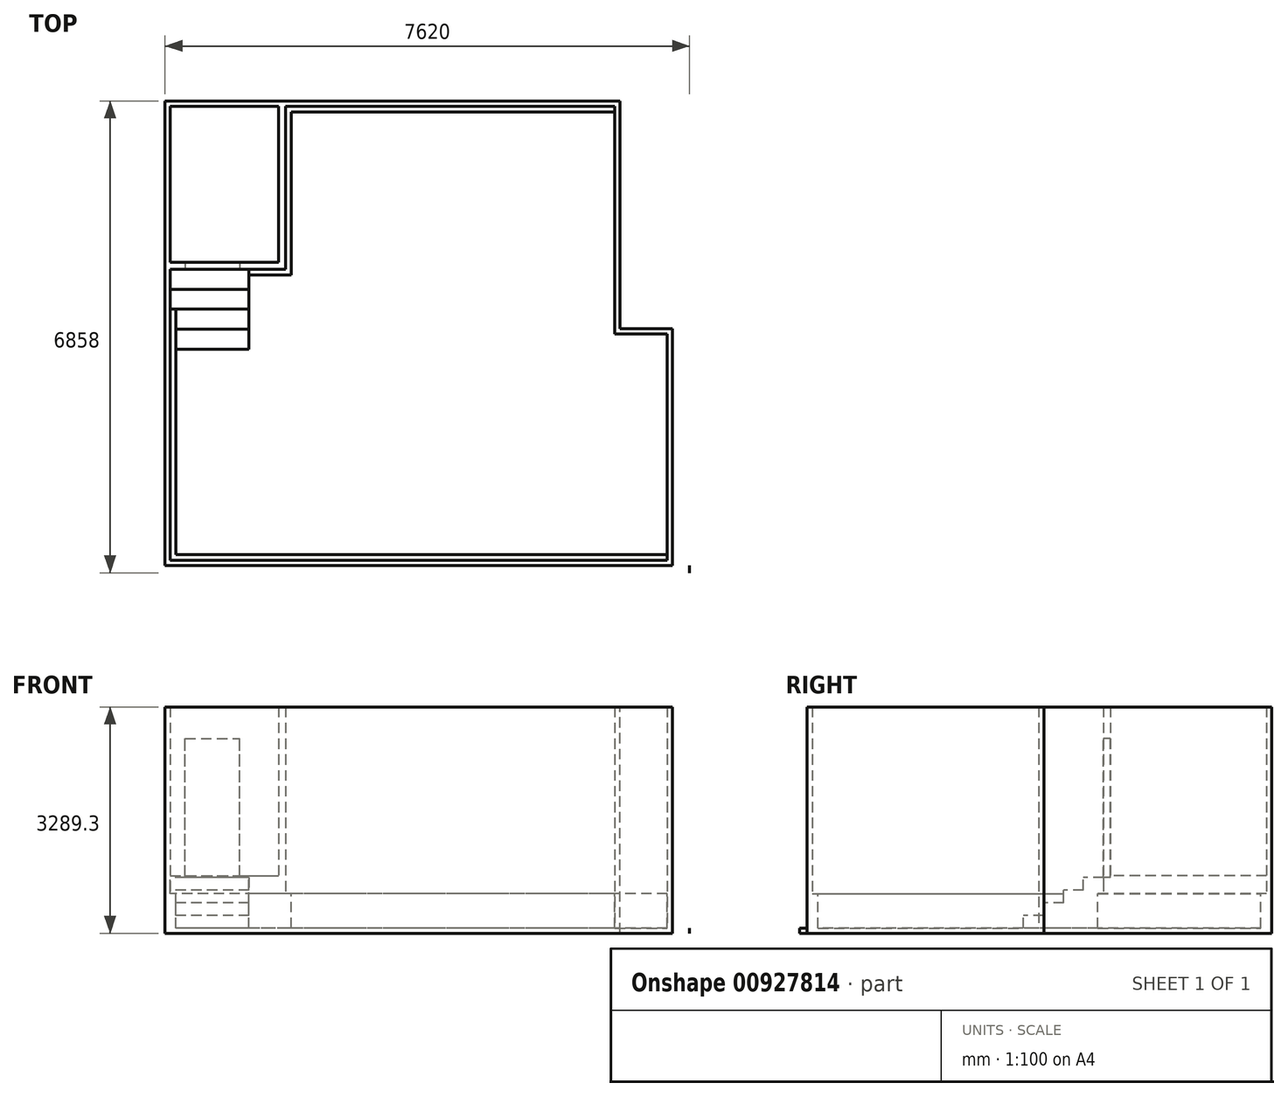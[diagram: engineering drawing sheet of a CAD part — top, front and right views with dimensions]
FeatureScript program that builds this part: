
annotation { "Feature Type Name" : "Feature", "Feature Type Description" : "" }
export const myFeature = defineFeature(function(context is Context, id is Id, definition is map)
    precondition{}
    {
        {
            var Q0;
            Q0=qCreatedBy(makeId("Top.planeOp"),FACE);
            var sketch = newSketch(context, id + "F0", { "sketchPlane" : qUnion([Q0])});
            skLineSegment(sketch, "E0.bottom", {"start": v(0, 0) * mm, "end": v(7620, 0) * mm});
            skLineSegment(sketch, "E0.top", {"start": v(0, -6858) * mm, "end": v(7620, -6858) * mm});
            skLineSegment(sketch, "E0.left", {"start": v(0, 0) * mm, "end": v(0, -6858) * mm});
            skLineSegment(sketch, "E0.right", {"start": v(7620, 0) * mm, "end": v(7620, -6858) * mm});
            skSolve(sketch);
        }
        {
            var Q0;
            Q0=makeQuery(id+"F0.imprint","IMPRINT",FACE,{"disambiguationData":[TD([[makeQuery(id+"F0.imprint","IMPRINT",EDGE,{"derivedFrom":sQuery(id+"F0.wireOp",EDGE,"E0.bottom")}),-1.0]])]});
            extrude(context, id + "F1", {"entities" : qUnion([Q0]), "oppositeDirection" : true, "depth" : 76.2 * mm, "offsetDistance" : 25.4 * mm});
        }
        {
            var Q0;
            Q0=makeQuery(id+"F1.opExtrude","CAP_FACE",FACE,{"disambiguationData":[OSD([sQuery(id+"F0.wireOp",EDGE,"E0.bottom"),sQuery(id+"F0.wireOp",EDGE,"E0.top"),sQuery(id+"F0.wireOp",EDGE,"E0.left"),sQuery(id+"F0.wireOp",EDGE,"E0.right")])],"isStart":true});
            var sketch = newSketch(context, id + "F2", { "sketchPlane" : qUnion([Q0])});
            skLineSegment(sketch, "E1.bottom", {"start": v(0, 0) * mm, "end": v(76.2, 0) * mm});
            skLineSegment(sketch, "E1.top", {"start": v(0, -6858) * mm, "end": v(76.2, -6858) * mm});
            skLineSegment(sketch, "E1.left", {"start": v(0, 0) * mm, "end": v(0, -6858) * mm});
            skLineSegment(sketch, "E1.right", {"start": v(76.2, 0) * mm, "end": v(76.2, -6858) * mm});
            skSolve(sketch);
        }
        {
            var Q0;
            Q0 = qSketchRegion(id + "F2", true);
            extrude(context, id + "F3", {"entities" : qUnion([Q0]), "operationType" : NewBodyOperationType.ADD, "depth" : 3213.1 * mm, "offsetDistance" : 25.4 * mm});
        }
        {
            var Q0;
            Q0=makeQuery(id+"F1.opExtrude","CAP_FACE",FACE,{"disambiguationData":[OSD([sQuery(id+"F0.wireOp",EDGE,"E0.bottom"),sQuery(id+"F0.wireOp",EDGE,"E0.top"),sQuery(id+"F0.wireOp",EDGE,"E0.left"),sQuery(id+"F0.wireOp",EDGE,"E0.right")])],"isStart":true});
            var sketch = newSketch(context, id + "F4", { "sketchPlane" : qUnion([Q0])});
            skLineSegment(sketch, "E2.bottom", {"start": v(76.2, 0) * mm, "end": v(7620, 0) * mm});
            skLineSegment(sketch, "E2.top", {"start": v(76.2, -76.2) * mm, "end": v(7620, -76.2) * mm});
            skLineSegment(sketch, "E2.left", {"start": v(76.2, 0) * mm, "end": v(76.2, -76.2) * mm});
            skLineSegment(sketch, "E2.right", {"start": v(7620, 0) * mm, "end": v(7620, -76.2) * mm});
            skSolve(sketch);
        }
        {
            var Q0;
            Q0 = qSketchRegion(id + "F4", true);
            extrude(context, id + "F5", {"entities" : qUnion([Q0]), "operationType" : NewBodyOperationType.ADD, "depth" : 3213.1 * mm, "offsetDistance" : 25.4 * mm});
        }
        {
            var Q0;
            Q0=makeQuery(id+"F1.opExtrude","CAP_FACE",FACE,{"disambiguationData":[OSD([sQuery(id+"F0.wireOp",EDGE,"E0.bottom"),sQuery(id+"F0.wireOp",EDGE,"E0.top"),sQuery(id+"F0.wireOp",EDGE,"E0.left"),sQuery(id+"F0.wireOp",EDGE,"E0.right")])],"isStart":true});
            var sketch = newSketch(context, id + "F6", { "sketchPlane" : qUnion([Q0])});
            skLineSegment(sketch, "E3.bottom", {"start": v(76.2, -76.2) * mm, "end": v(1752.6, -76.2) * mm});
            skLineSegment(sketch, "E3.top", {"start": v(76.2, -2444.75) * mm, "end": v(1752.6, -2444.75) * mm});
            skLineSegment(sketch, "E3.left", {"start": v(76.2, -76.2) * mm, "end": v(76.2, -2444.75) * mm});
            skLineSegment(sketch, "E3.right", {"start": v(1752.6, -76.2) * mm, "end": v(1752.6, -2444.75) * mm});
            skSolve(sketch);
        }
        {
            var Q0;
            Q0=makeQuery(id+"F6.imprint","IMPRINT",FACE,{"disambiguationData":[TD([[makeQuery(id+"F6.imprint","IMPRINT",EDGE,{"derivedFrom":sQuery(id+"F6.wireOp",EDGE,"E3.bottom")}),-1.0]])]});
            extrude(context, id + "F7", {"entities" : qUnion([Q0]), "operationType" : NewBodyOperationType.ADD, "depth" : 736.6 * mm, "offsetDistance" : 25.4 * mm});
        }
        {
            var Q0;
            Q0=makeQuery(id+"F7.opExtrude","CAP_FACE",FACE,{"disambiguationData":[OSD([sQuery(id+"F6.wireOp",EDGE,"E3.bottom"),sQuery(id+"F6.wireOp",EDGE,"E3.top"),sQuery(id+"F6.wireOp",EDGE,"E3.left"),sQuery(id+"F6.wireOp",EDGE,"E3.right")])],"isStart":false});
            var sketch = newSketch(context, id + "F8", { "sketchPlane" : qUnion([Q0])});
            skSolve(sketch);
        }
        {
            var Q0;
            Q0=makeQuery(id+"F8.imprint","IMPRINT",FACE,{"disambiguationData":[TD([[makeQuery(id+"F8.imprint","IMPRINT",EDGE,{"derivedFrom":makeQuery(id+"F7.opExtrude","CAP_EDGE",EDGE,{"disambiguationData":[OSD([sQuery(id+"F6.wireOp",EDGE,"E3.top")])],"isStart":false})}),1.0]])]});
            extrude(context, id + "F9", {"entities" : qUnion([Q0]), "operationType" : NewBodyOperationType.ADD, "depth" : 25.4 * mm, "offsetDistance" : 25.4 * mm});
        }
        {
            var Q0;
            Q0=makeQuery(id+"F9.opExtrude","CAP_FACE",FACE,{"disambiguationData":[OSD([sQuery(id+"F6.wireOp",EDGE,"E3.bottom"),sQuery(id+"F6.wireOp",EDGE,"E3.top"),sQuery(id+"F6.wireOp",EDGE,"E3.left"),sQuery(id+"F6.wireOp",EDGE,"E3.right")])],"isStart":false});
            var sketch = newSketch(context, id + "F10", { "sketchPlane" : qUnion([Q0])});
            skLineSegment(sketch, "E4.bottom", {"start": v(76.2, -2444.75) * mm, "end": v(1752.6, -2444.75) * mm});
            skLineSegment(sketch, "E4.top", {"start": v(76.2, -2343.15) * mm, "end": v(1752.6, -2343.15) * mm});
            skLineSegment(sketch, "E4.left", {"start": v(76.2, -2444.75) * mm, "end": v(76.2, -2343.15) * mm});
            skLineSegment(sketch, "E4.right", {"start": v(1752.6, -2444.75) * mm, "end": v(1752.6, -2343.15) * mm});
            skLineSegment(sketch, "E5.bottom", {"start": v(1752.6, -2343.15) * mm, "end": v(1651, -2343.15) * mm});
            skLineSegment(sketch, "E5.top", {"start": v(1752.6, -76.2) * mm, "end": v(1651, -76.2) * mm});
            skLineSegment(sketch, "E5.left", {"start": v(1752.6, -2343.15) * mm, "end": v(1752.6, -76.2) * mm});
            skLineSegment(sketch, "E5.right", {"start": v(1651, -2343.15) * mm, "end": v(1651, -76.2) * mm});
            skSolve(sketch);
        }
        {
            var Q0;
            Q0 = qSketchRegion(id + "F10", true);
            extrude(context, id + "F11", {"entities" : qUnion([Q0]), "operationType" : NewBodyOperationType.ADD, "depth" : 2451.1 * mm, "offsetDistance" : 25.4 * mm});
        }
        {
            var Q0;
            {var subQ0=sQuery(id+"F2.wireOp",EDGE,"E1.right");var subQ2=sQuery(id+"F0.wireOp",EDGE,"E0.top");Q0=makeQuery(id+"F11.boolean.opBoolean","SPLIT",FACE,{"disambiguationData":[TD([makeQuery(id+"F1.opExtrude","SWEPT_FACE",FACE,{"disambiguationData":[OSD([subQ2])]})])],"derivedFrom":makeQuery(id+"F3.opExtrude","SWEPT_FACE",FACE,{"disambiguationData":[OSD([subQ0])]})});}
            var sketch = newSketch(context, id + "F12", { "sketchPlane" : qUnion([Q0])});
            skLineSegment(sketch, "E6.bottom", {"start": v(-2444.75, 0) * mm, "end": v(-2736.85, 0) * mm});
            skLineSegment(sketch, "E6.top", {"start": v(-2444.75, 736.6) * mm, "end": v(-2736.85, 736.6) * mm});
            skLineSegment(sketch, "E6.left", {"start": v(-2444.75, 0) * mm, "end": v(-2444.75, 736.6) * mm});
            skLineSegment(sketch, "E6.right", {"start": v(-2736.85, 552.45) * mm, "end": v(-2736.85, 736.6) * mm});
            skLineSegment(sketch, "E7.bottom", {"start": v(-2736.85, 0) * mm, "end": v(-3022.6, 0) * mm});
            skLineSegment(sketch, "E7.top", {"start": v(-2736.85, 552.45) * mm, "end": v(-3022.6, 552.45) * mm});
            skLineSegment(sketch, "E7.right", {"start": v(-3022.6, 368.3) * mm, "end": v(-3022.6, 552.45) * mm});
            skLineSegment(sketch, "E8.bottom", {"start": v(-3022.6, 0) * mm, "end": v(-3314.7, 0) * mm});
            skLineSegment(sketch, "E8.top", {"start": v(-3022.6, 368.3) * mm, "end": v(-3314.7, 368.3) * mm});
            skLineSegment(sketch, "E8.right", {"start": v(-3314.7, 184.15) * mm, "end": v(-3314.7, 368.3) * mm});
            skLineSegment(sketch, "E9.bottom", {"start": v(-3314.7, 0) * mm, "end": v(-3606.8, 0) * mm});
            skLineSegment(sketch, "E9.top", {"start": v(-3314.7, 184.15) * mm, "end": v(-3606.8, 184.15) * mm});
            skLineSegment(sketch, "E9.right", {"start": v(-3606.8, 0) * mm, "end": v(-3606.8, 184.15) * mm});
            skSolve(sketch);
        }
        {
            var Q0;
            Q0=makeQuery(id+"F12.imprint","IMPRINT",FACE,{"disambiguationData":[TD([[makeQuery(id+"F12.imprint","IMPRINT",EDGE,{"derivedFrom":sQuery(id+"F12.wireOp",EDGE,"E6.bottom")}),-1.0]])]});
            extrude(context, id + "F13", {"entities" : qUnion([Q0]), "operationType" : NewBodyOperationType.ADD, "depth" : 1143 * mm, "offsetDistance" : 25.4 * mm});
        }
        {
            var Q0;
            Q0=makeQuery(id+"F1.opExtrude","CAP_FACE",FACE,{"disambiguationData":[OSD([sQuery(id+"F0.wireOp",EDGE,"E0.bottom"),sQuery(id+"F0.wireOp",EDGE,"E0.top"),sQuery(id+"F0.wireOp",EDGE,"E0.left"),sQuery(id+"F0.wireOp",EDGE,"E0.right")])],"isStart":true});
            var sketch = newSketch(context, id + "F14", { "sketchPlane" : qUnion([Q0])});
            skLineSegment(sketch, "E10.bottom", {"start": v(6534.15, -76.2) * mm, "end": v(6610.35, -76.2) * mm});
            skLineSegment(sketch, "E10.top", {"start": v(6534.15, -3384.55) * mm, "end": v(6610.35, -3384.55) * mm});
            skLineSegment(sketch, "E10.left", {"start": v(6534.15, -76.2) * mm, "end": v(6534.15, -3384.55) * mm});
            skLineSegment(sketch, "E10.right", {"start": v(6610.35, -76.2) * mm, "end": v(6610.35, -3384.55) * mm});
            skSolve(sketch);
        }
        {
            var Q0;
            Q0 = qSketchRegion(id + "F14", true);
            extrude(context, id + "F15", {"entities" : qUnion([Q0]), "operationType" : NewBodyOperationType.ADD, "depth" : 3213.1 * mm, "offsetDistance" : 25.4 * mm});
        }
        {
            var Q0;
            Q0=makeQuery(id+"F1.opExtrude","CAP_FACE",FACE,{"disambiguationData":[OSD([sQuery(id+"F0.wireOp",EDGE,"E0.bottom"),sQuery(id+"F0.wireOp",EDGE,"E0.top"),sQuery(id+"F0.wireOp",EDGE,"E0.left"),sQuery(id+"F0.wireOp",EDGE,"E0.right")])],"isStart":true});
            var sketch = newSketch(context, id + "F16", { "sketchPlane" : qUnion([Q0])});
            skLineSegment(sketch, "E11.bottom", {"start": v(6610.35, -3384.55) * mm, "end": v(7620, -3384.55) * mm});
            skLineSegment(sketch, "E11.top", {"start": v(6610.35, -3308.35) * mm, "end": v(7620, -3308.35) * mm});
            skLineSegment(sketch, "E11.left", {"start": v(6610.35, -3384.55) * mm, "end": v(6610.35, -3308.35) * mm});
            skLineSegment(sketch, "E11.right", {"start": v(7620, -3384.55) * mm, "end": v(7620, -3308.35) * mm});
            skSolve(sketch);
        }
        {
            var Q0;
            Q0 = qSketchRegion(id + "F16", true);
            extrude(context, id + "F17", {"entities" : qUnion([Q0]), "operationType" : NewBodyOperationType.ADD, "depth" : 3213.1 * mm, "offsetDistance" : 25.4 * mm});
        }
        {
            var Q0;
            {var subQ1=sQuery(id+"F0.wireOp",EDGE,"E0.top");var subQ3=sQuery(id+"F0.wireOp",EDGE,"E0.right");Q0=makeQuery(id+"F17.boolean.opBoolean","SPLIT",FACE,{"disambiguationData":[TD([makeQuery(id+"F1.opExtrude","SWEPT_FACE",FACE,{"disambiguationData":[OSD([subQ1])]})])],"derivedFrom":makeQuery(id+"F1.opExtrude","CAP_FACE",FACE,{"disambiguationData":[OSD([sQuery(id+"F0.wireOp",EDGE,"E0.bottom"),subQ1,sQuery(id+"F0.wireOp",EDGE,"E0.left"),subQ3])],"isStart":true})});}
            var sketch = newSketch(context, id + "F18", { "sketchPlane" : qUnion([Q0])});
            skLineSegment(sketch, "E12.bottom", {"start": v(7296.15, -3384.55) * mm, "end": v(7372.35, -3384.55) * mm});
            skLineSegment(sketch, "E12.top", {"start": v(7296.15, -6858) * mm, "end": v(7372.35, -6858) * mm});
            skLineSegment(sketch, "E12.left", {"start": v(7296.15, -3384.55) * mm, "end": v(7296.15, -6858) * mm});
            skLineSegment(sketch, "E12.right", {"start": v(7372.35, -3384.55) * mm, "end": v(7372.35, -6858) * mm});
            skSolve(sketch);
        }
        {
            var Q0;
            Q0 = qSketchRegion(id + "F18", true);
            extrude(context, id + "F19", {"entities" : qUnion([Q0]), "operationType" : NewBodyOperationType.ADD, "depth" : 3213.1 * mm, "offsetDistance" : 25.4 * mm});
        }
        {
            var Q0;
            {var subQ7=sQuery(id+"F0.wireOp",EDGE,"E0.top");var subQ8=makeQuery(id+"F1.opExtrude","SWEPT_FACE",FACE,{"disambiguationData":[OSD([subQ7])]});var subQ10=makeQuery(id+"F3.opExtrude","SWEPT_FACE",FACE,{"disambiguationData":[OSD([sQuery(id+"F2.wireOp",EDGE,"E1.right")])]});var subQ15=sQuery(id+"F0.wireOp",EDGE,"E0.right");Q0=makeQuery(id+"F19.boolean.opBoolean","SPLIT",FACE,{"disambiguationData":[TD([subQ10])],"derivedFrom":makeQuery(id+"F17.boolean.opBoolean","SPLIT",FACE,{"disambiguationData":[TD([subQ8])],"derivedFrom":makeQuery(id+"F1.opExtrude","CAP_FACE",FACE,{"disambiguationData":[OSD([sQuery(id+"F0.wireOp",EDGE,"E0.bottom"),subQ7,sQuery(id+"F0.wireOp",EDGE,"E0.left"),subQ15])],"isStart":true})})});}
            var sketch = newSketch(context, id + "F20", { "sketchPlane" : qUnion([Q0])});
            skLineSegment(sketch, "E13.bottom", {"start": v(7296.15, -6750.05) * mm, "end": v(76.2, -6750.05) * mm});
            skLineSegment(sketch, "E13.top", {"start": v(7296.15, -6673.85) * mm, "end": v(76.2, -6673.85) * mm});
            skLineSegment(sketch, "E13.left", {"start": v(7296.15, -6750.05) * mm, "end": v(7296.15, -6673.85) * mm});
            skLineSegment(sketch, "E13.right", {"start": v(76.2, -6750.05) * mm, "end": v(76.2, -6673.85) * mm});
            skSolve(sketch);
        }
        {
            var Q0;
            Q0 = qSketchRegion(id + "F20", true);
            extrude(context, id + "F21", {"entities" : qUnion([Q0]), "operationType" : NewBodyOperationType.ADD, "depth" : 3213.1 * mm, "offsetDistance" : 25.4 * mm});
        }
        {
            var Q0;
            Q0=makeQuery(id+"F21.boolean.opBoolean","MERGE",FACE,{"derivedFrom":[makeQuery(id+"F19.boolean.opBoolean","MERGE",FACE,{"derivedFrom":[makeQuery(id+"F17.boolean.opBoolean","MERGE",FACE,{"derivedFrom":[makeQuery(id+"F15.boolean.opBoolean","MERGE",FACE,{"derivedFrom":[makeQuery(id+"F11.boolean.opBoolean","MERGE",FACE,{"derivedFrom":[makeQuery(id+"F5.boolean.opBoolean","MERGE",FACE,{"derivedFrom":[makeQuery(id+"F3.opExtrude","CAP_FACE",FACE,{"disambiguationData":[OSD([sQuery(id+"F2.wireOp",EDGE,"E1.bottom"),sQuery(id+"F2.wireOp",EDGE,"E1.top"),sQuery(id+"F2.wireOp",EDGE,"E1.left"),sQuery(id+"F2.wireOp",EDGE,"E1.right")])],"isStart":false}),makeQuery(id+"F5.opExtrude","CAP_FACE",FACE,{"disambiguationData":[OSD([sQuery(id+"F4.wireOp",EDGE,"E2.bottom"),sQuery(id+"F4.wireOp",EDGE,"E2.top"),sQuery(id+"F4.wireOp",EDGE,"E2.left"),sQuery(id+"F4.wireOp",EDGE,"E2.right")])],"isStart":false})]}),makeQuery(id+"F11.opExtrude","CAP_FACE",FACE,{"disambiguationData":[OSD([sQuery(id+"F10.wireOp",EDGE,"E4.bottom"),sQuery(id+"F10.wireOp",EDGE,"E4.top"),sQuery(id+"F10.wireOp",EDGE,"E4.left"),sQuery(id+"F10.wireOp",EDGE,"E4.right"),sQuery(id+"F10.wireOp",EDGE,"E5.top"),sQuery(id+"F10.wireOp",EDGE,"E5.left"),sQuery(id+"F10.wireOp",EDGE,"E5.right")])],"isStart":false})]}),makeQuery(id+"F15.opExtrude","CAP_FACE",FACE,{"disambiguationData":[OSD([sQuery(id+"F14.wireOp",EDGE,"E10.bottom"),sQuery(id+"F14.wireOp",EDGE,"E10.top"),sQuery(id+"F14.wireOp",EDGE,"E10.left"),sQuery(id+"F14.wireOp",EDGE,"E10.right")])],"isStart":false})]}),makeQuery(id+"F17.opExtrude","CAP_FACE",FACE,{"disambiguationData":[OSD([sQuery(id+"F16.wireOp",EDGE,"E11.bottom"),sQuery(id+"F16.wireOp",EDGE,"E11.top"),sQuery(id+"F16.wireOp",EDGE,"E11.left"),sQuery(id+"F16.wireOp",EDGE,"E11.right")])],"isStart":false})]}),makeQuery(id+"F19.opExtrude","CAP_FACE",FACE,{"disambiguationData":[OSD([sQuery(id+"F18.wireOp",EDGE,"E12.bottom"),sQuery(id+"F18.wireOp",EDGE,"E12.top"),sQuery(id+"F18.wireOp",EDGE,"E12.left"),sQuery(id+"F18.wireOp",EDGE,"E12.right")])],"isStart":false})]}),makeQuery(id+"F21.opExtrude","CAP_FACE",FACE,{"disambiguationData":[OSD([sQuery(id+"F20.wireOp",EDGE,"E13.bottom"),sQuery(id+"F20.wireOp",EDGE,"E13.top"),sQuery(id+"F20.wireOp",EDGE,"E13.left"),sQuery(id+"F20.wireOp",EDGE,"E13.right")])],"isStart":false})]});
            var sketch = newSketch(context, id + "F22", { "sketchPlane" : qUnion([Q0])});
            skLineSegment(sketch, "E14.bottom", {"start": v(0, -6858) * mm, "end": v(7614.91, -6858) * mm});
            skLineSegment(sketch, "E14.top", {"start": v(0, -6750.05) * mm, "end": v(7614.91, -6750.05) * mm});
            skLineSegment(sketch, "E14.left", {"start": v(0, -6858) * mm, "end": v(0, -6750.05) * mm});
            skLineSegment(sketch, "E14.right", {"start": v(7614.91, -6858) * mm, "end": v(7614.91, -6750.05) * mm});
            skSolve(sketch);
        }
        {
            var Q0;
            Q0 = qSketchRegion(id + "F22", true);
            extrude(context, id + "F23", {"entities" : qUnion([Q0]), "operationType" : NewBodyOperationType.REMOVE, "oppositeDirection" : true, "depth" : 3289.3 * mm, "offsetDistance" : 25.4 * mm});
        }
        {
            var Q0;
            Q0=makeQuery(id+"F21.boolean.opBoolean","MERGE",FACE,{"derivedFrom":[makeQuery(id+"F19.boolean.opBoolean","MERGE",FACE,{"derivedFrom":[makeQuery(id+"F17.boolean.opBoolean","MERGE",FACE,{"derivedFrom":[makeQuery(id+"F15.boolean.opBoolean","MERGE",FACE,{"derivedFrom":[makeQuery(id+"F11.boolean.opBoolean","MERGE",FACE,{"derivedFrom":[makeQuery(id+"F5.boolean.opBoolean","MERGE",FACE,{"derivedFrom":[makeQuery(id+"F3.opExtrude","CAP_FACE",FACE,{"disambiguationData":[OSD([sQuery(id+"F2.wireOp",EDGE,"E1.bottom"),sQuery(id+"F2.wireOp",EDGE,"E1.top"),sQuery(id+"F2.wireOp",EDGE,"E1.left"),sQuery(id+"F2.wireOp",EDGE,"E1.right")])],"isStart":false}),makeQuery(id+"F5.opExtrude","CAP_FACE",FACE,{"disambiguationData":[OSD([sQuery(id+"F4.wireOp",EDGE,"E2.bottom"),sQuery(id+"F4.wireOp",EDGE,"E2.top"),sQuery(id+"F4.wireOp",EDGE,"E2.left"),sQuery(id+"F4.wireOp",EDGE,"E2.right")])],"isStart":false})]}),makeQuery(id+"F11.opExtrude","CAP_FACE",FACE,{"disambiguationData":[OSD([sQuery(id+"F10.wireOp",EDGE,"E4.bottom"),sQuery(id+"F10.wireOp",EDGE,"E4.top"),sQuery(id+"F10.wireOp",EDGE,"E4.left"),sQuery(id+"F10.wireOp",EDGE,"E4.right"),sQuery(id+"F10.wireOp",EDGE,"E5.top"),sQuery(id+"F10.wireOp",EDGE,"E5.left"),sQuery(id+"F10.wireOp",EDGE,"E5.right")])],"isStart":false})]}),makeQuery(id+"F15.opExtrude","CAP_FACE",FACE,{"disambiguationData":[OSD([sQuery(id+"F14.wireOp",EDGE,"E10.bottom"),sQuery(id+"F14.wireOp",EDGE,"E10.top"),sQuery(id+"F14.wireOp",EDGE,"E10.left"),sQuery(id+"F14.wireOp",EDGE,"E10.right")])],"isStart":false})]}),makeQuery(id+"F17.opExtrude","CAP_FACE",FACE,{"disambiguationData":[OSD([sQuery(id+"F16.wireOp",EDGE,"E11.bottom"),sQuery(id+"F16.wireOp",EDGE,"E11.top"),sQuery(id+"F16.wireOp",EDGE,"E11.left"),sQuery(id+"F16.wireOp",EDGE,"E11.right")])],"isStart":false})]}),makeQuery(id+"F19.opExtrude","CAP_FACE",FACE,{"disambiguationData":[OSD([sQuery(id+"F18.wireOp",EDGE,"E12.bottom"),sQuery(id+"F18.wireOp",EDGE,"E12.top"),sQuery(id+"F18.wireOp",EDGE,"E12.left"),sQuery(id+"F18.wireOp",EDGE,"E12.right")])],"isStart":false})]}),makeQuery(id+"F21.opExtrude","CAP_FACE",FACE,{"disambiguationData":[OSD([sQuery(id+"F20.wireOp",EDGE,"E13.bottom"),sQuery(id+"F20.wireOp",EDGE,"E13.top"),sQuery(id+"F20.wireOp",EDGE,"E13.left"),sQuery(id+"F20.wireOp",EDGE,"E13.right")])],"isStart":false})]});
            var sketch = newSketch(context, id + "F24", { "sketchPlane" : qUnion([Q0])});
            skLineSegment(sketch, "E15.bottom", {"start": v(7372.35, -6750.05) * mm, "end": v(7620, -6750.05) * mm});
            skLineSegment(sketch, "E15.top", {"start": v(7372.35, 0) * mm, "end": v(7620, 0) * mm});
            skLineSegment(sketch, "E15.left", {"start": v(7372.35, -6750.05) * mm, "end": v(7372.35, 0) * mm});
            skLineSegment(sketch, "E15.right", {"start": v(7620, -6750.05) * mm, "end": v(7620, 0) * mm});
            skSolve(sketch);
        }
        {
            var Q0;
            Q0 = qSketchRegion(id + "F24", true);
            extrude(context, id + "F25", {"entities" : qUnion([Q0]), "operationType" : NewBodyOperationType.REMOVE, "oppositeDirection" : true, "depth" : 3289.3 * mm, "offsetDistance" : 25.4 * mm});
        }
        {
            var Q0;
            Q0=makeQuery(id+"F21.boolean.opBoolean","MERGE",FACE,{"derivedFrom":[makeQuery(id+"F19.boolean.opBoolean","MERGE",FACE,{"derivedFrom":[makeQuery(id+"F17.boolean.opBoolean","MERGE",FACE,{"derivedFrom":[makeQuery(id+"F15.boolean.opBoolean","MERGE",FACE,{"derivedFrom":[makeQuery(id+"F11.boolean.opBoolean","MERGE",FACE,{"derivedFrom":[makeQuery(id+"F5.boolean.opBoolean","MERGE",FACE,{"derivedFrom":[makeQuery(id+"F3.opExtrude","CAP_FACE",FACE,{"disambiguationData":[OSD([sQuery(id+"F2.wireOp",EDGE,"E1.bottom"),sQuery(id+"F2.wireOp",EDGE,"E1.top"),sQuery(id+"F2.wireOp",EDGE,"E1.left"),sQuery(id+"F2.wireOp",EDGE,"E1.right")])],"isStart":false}),makeQuery(id+"F5.opExtrude","CAP_FACE",FACE,{"disambiguationData":[OSD([sQuery(id+"F4.wireOp",EDGE,"E2.bottom"),sQuery(id+"F4.wireOp",EDGE,"E2.top"),sQuery(id+"F4.wireOp",EDGE,"E2.left"),sQuery(id+"F4.wireOp",EDGE,"E2.right")])],"isStart":false})]}),makeQuery(id+"F11.opExtrude","CAP_FACE",FACE,{"disambiguationData":[OSD([sQuery(id+"F10.wireOp",EDGE,"E4.bottom"),sQuery(id+"F10.wireOp",EDGE,"E4.top"),sQuery(id+"F10.wireOp",EDGE,"E4.left"),sQuery(id+"F10.wireOp",EDGE,"E4.right"),sQuery(id+"F10.wireOp",EDGE,"E5.top"),sQuery(id+"F10.wireOp",EDGE,"E5.left"),sQuery(id+"F10.wireOp",EDGE,"E5.right")])],"isStart":false})]}),makeQuery(id+"F15.opExtrude","CAP_FACE",FACE,{"disambiguationData":[OSD([sQuery(id+"F14.wireOp",EDGE,"E10.bottom"),sQuery(id+"F14.wireOp",EDGE,"E10.top"),sQuery(id+"F14.wireOp",EDGE,"E10.left"),sQuery(id+"F14.wireOp",EDGE,"E10.right")])],"isStart":false})]}),makeQuery(id+"F17.opExtrude","CAP_FACE",FACE,{"disambiguationData":[OSD([sQuery(id+"F16.wireOp",EDGE,"E11.bottom"),sQuery(id+"F16.wireOp",EDGE,"E11.top"),sQuery(id+"F16.wireOp",EDGE,"E11.left"),sQuery(id+"F16.wireOp",EDGE,"E11.right")])],"isStart":false})]}),makeQuery(id+"F19.opExtrude","CAP_FACE",FACE,{"disambiguationData":[OSD([sQuery(id+"F18.wireOp",EDGE,"E12.bottom"),sQuery(id+"F18.wireOp",EDGE,"E12.top"),sQuery(id+"F18.wireOp",EDGE,"E12.left"),sQuery(id+"F18.wireOp",EDGE,"E12.right")])],"isStart":false})]}),makeQuery(id+"F21.opExtrude","CAP_FACE",FACE,{"disambiguationData":[OSD([sQuery(id+"F20.wireOp",EDGE,"E13.bottom"),sQuery(id+"F20.wireOp",EDGE,"E13.top"),sQuery(id+"F20.wireOp",EDGE,"E13.left"),sQuery(id+"F20.wireOp",EDGE,"E13.right")])],"isStart":false})]});
            var sketch = newSketch(context, id + "F26", { "sketchPlane" : qUnion([Q0])});
            skLineSegment(sketch, "E16.bottom", {"start": v(6610.35, -3308.35) * mm, "end": v(7372.35, -3308.35) * mm});
            skLineSegment(sketch, "E16.top", {"start": v(6610.35, 0) * mm, "end": v(7372.35, 0) * mm});
            skLineSegment(sketch, "E16.left", {"start": v(6610.35, -3308.35) * mm, "end": v(6610.35, 0) * mm});
            skLineSegment(sketch, "E16.right", {"start": v(7372.35, -3308.35) * mm, "end": v(7372.35, 0) * mm});
            skSolve(sketch);
        }
        {
            var Q0;
            Q0 = qSketchRegion(id + "F26", true);
            extrude(context, id + "F27", {"entities" : qUnion([Q0]), "operationType" : NewBodyOperationType.REMOVE, "oppositeDirection" : true, "depth" : 3289.3 * mm, "offsetDistance" : 25.4 * mm});
        }
        {
            var Q0;
            {var subQ0=sQuery(id+"F6.wireOp",EDGE,"E3.top");Q0=makeQuery(id+"F11.boolean.opBoolean","MERGE",FACE,{"derivedFrom":[makeQuery(id+"F9.boolean.opBoolean","MERGE",FACE,{"derivedFrom":[makeQuery(id+"F7.opExtrude","SWEPT_FACE",FACE,{"disambiguationData":[OSD([subQ0])]}),makeQuery(id+"F9.opExtrude","SWEPT_FACE",FACE,{"disambiguationData":[OSD([subQ0])]})]}),makeQuery(id+"F11.opExtrude","SWEPT_FACE",FACE,{"disambiguationData":[OSD([sQuery(id+"F10.wireOp",EDGE,"E4.bottom")])]})]});}
            var sketch = newSketch(context, id + "F28", { "sketchPlane" : qUnion([Q0])});
            skLineSegment(sketch, "E17.bottom", {"start": v(292.1, 736.6) * mm, "end": v(1085.85, 736.6) * mm});
            skLineSegment(sketch, "E17.top", {"start": v(292.1, 2755.9) * mm, "end": v(1085.85, 2755.9) * mm});
            skLineSegment(sketch, "E17.left", {"start": v(292.1, 736.6) * mm, "end": v(292.1, 2755.9) * mm});
            skLineSegment(sketch, "E17.right", {"start": v(1085.85, 736.6) * mm, "end": v(1085.85, 2755.9) * mm});
            skSolve(sketch);
        }
        {
            var Q0;
            Q0 = qSketchRegion(id + "F28", true);
            extrude(context, id + "F29", {"entities" : qUnion([Q0]), "operationType" : NewBodyOperationType.REMOVE, "oppositeDirection" : true, "depth" : 101.6 * mm, "offsetDistance" : 25.4 * mm});
        }
        {
            var Q0;
            {var subQ0=sQuery(id+"F6.wireOp",EDGE,"E3.right");Q0=makeQuery(id+"F11.boolean.opBoolean","MERGE",FACE,{"derivedFrom":[makeQuery(id+"F9.boolean.opBoolean","MERGE",FACE,{"derivedFrom":[makeQuery(id+"F7.opExtrude","SWEPT_FACE",FACE,{"disambiguationData":[OSD([subQ0])]}),makeQuery(id+"F9.opExtrude","SWEPT_FACE",FACE,{"disambiguationData":[OSD([subQ0])]})]}),makeQuery(id+"F11.opExtrude","SWEPT_FACE",FACE,{"disambiguationData":[OSD([sQuery(id+"F10.wireOp",EDGE,"E4.right"),sQuery(id+"F10.wireOp",EDGE,"E5.left")])]})]});}
            var sketch = newSketch(context, id + "F30", { "sketchPlane" : qUnion([Q0])});
            skLineSegment(sketch, "E18.bottom", {"start": v(-76.2, 0) * mm, "end": v(-158.75, 0) * mm});
            skLineSegment(sketch, "E18.top", {"start": v(-76.2, 501.65) * mm, "end": v(-158.75, 501.65) * mm});
            skLineSegment(sketch, "E18.left", {"start": v(-76.2, 0) * mm, "end": v(-76.2, 501.65) * mm});
            skLineSegment(sketch, "E18.right", {"start": v(-158.75, 0) * mm, "end": v(-158.75, 501.65) * mm});
            skSolve(sketch);
        }
        {
            var Q0;
            Q0 = qSketchRegion(id + "F30", true);
            var Q1;
            Q1=makeQuery(id+"F15.opExtrude","SWEPT_FACE",FACE,{"disambiguationData":[OSD([sQuery(id+"F14.wireOp",EDGE,"E10.left")])]});
            extrude(context, id + "F31", {"entities" : qUnion([Q0, Q1]), "operationType" : NewBodyOperationType.ADD, "endBound" : BoundingType.UP_TO_NEXT, "depth" : 25.4 * mm, "offsetDistance" : 25.4 * mm});
        }
        {
            var Q0;
            {var subQ0=sQuery(id+"F2.wireOp",EDGE,"E1.right");var subQ5=sQuery(id+"F6.wireOp",EDGE,"E3.top");var subQ6=makeQuery(id+"F7.opExtrude","SWEPT_FACE",FACE,{"disambiguationData":[OSD([subQ5])]});var subQ9=sQuery(id+"F0.wireOp",EDGE,"E0.top");Q0=makeQuery(id+"F21.boolean.opBoolean","SPLIT",FACE,{"disambiguationData":[TD([subQ6])],"derivedFrom":makeQuery(id+"F11.boolean.opBoolean","SPLIT",FACE,{"disambiguationData":[TD([makeQuery(id+"F1.opExtrude","SWEPT_FACE",FACE,{"disambiguationData":[OSD([subQ9])]})])],"derivedFrom":makeQuery(id+"F3.opExtrude","SWEPT_FACE",FACE,{"disambiguationData":[OSD([subQ0])]})})});}
            var sketch = newSketch(context, id + "F32", { "sketchPlane" : qUnion([Q0])});
            skLineSegment(sketch, "E19.bottom", {"start": v(-6673.85, 0) * mm, "end": v(-2609.85, 0) * mm});
            skLineSegment(sketch, "E19.top", {"start": v(-6673.85, 501.65) * mm, "end": v(-2609.85, 501.65) * mm});
            skLineSegment(sketch, "E19.left", {"start": v(-6673.85, 0) * mm, "end": v(-6673.85, 501.65) * mm});
            skLineSegment(sketch, "E19.right", {"start": v(-2609.85, 0) * mm, "end": v(-2609.85, 501.65) * mm});
            skSolve(sketch);
        }
        {
            var Q0;
            Q0 = qSketchRegion(id + "F32", true);
            extrude(context, id + "F33", {"entities" : qUnion([Q0]), "operationType" : NewBodyOperationType.ADD, "depth" : 82.55 * mm, "offsetDistance" : 25.4 * mm});
        }
        {
            var Q0;
            Q0=makeQuery(id+"F31.opExtrude","SWEPT_FACE",FACE,{"disambiguationData":[OSD([sQuery(id+"F30.wireOp",EDGE,"E18.right")])]});
            var sketch = newSketch(context, id + "F34", { "sketchPlane" : qUnion([Q0])});
            skLineSegment(sketch, "E20.bottom", {"start": v(1752.6, 0) * mm, "end": v(1835.15, 0) * mm});
            skLineSegment(sketch, "E20.top", {"start": v(1752.6, 501.65) * mm, "end": v(1835.15, 501.65) * mm});
            skLineSegment(sketch, "E20.left", {"start": v(1752.6, 0) * mm, "end": v(1752.6, 501.65) * mm});
            skLineSegment(sketch, "E20.right", {"start": v(1835.15, 0) * mm, "end": v(1835.15, 501.65) * mm});
            skSolve(sketch);
        }
        {
            var Q0;
            Q0 = qSketchRegion(id + "F34", true);
            var Q1;
            {var subQ0=sQuery(id+"F6.wireOp",EDGE,"E3.top");Q1=makeQuery(id+"F11.boolean.opBoolean","MERGE",FACE,{"derivedFrom":[makeQuery(id+"F9.boolean.opBoolean","MERGE",FACE,{"derivedFrom":[makeQuery(id+"F7.opExtrude","SWEPT_FACE",FACE,{"disambiguationData":[OSD([subQ0])]}),makeQuery(id+"F9.opExtrude","SWEPT_FACE",FACE,{"disambiguationData":[OSD([subQ0])]})]}),makeQuery(id+"F11.opExtrude","SWEPT_FACE",FACE,{"disambiguationData":[OSD([sQuery(id+"F10.wireOp",EDGE,"E4.bottom")])]})]});}
            extrude(context, id + "F35", {"entities" : qUnion([Q0]), "operationType" : NewBodyOperationType.ADD, "endBound" : BoundingType.UP_TO_SURFACE, "depth" : 25.4 * mm, "endBoundEntityFace" : qUnion([Q1]), "offsetDistance" : 25.4 * mm});
        }
        {
            var Q0;
            Q0=makeQuery(id+"F13.opExtrude","CAP_FACE",FACE,{"disambiguationData":[OSD([sQuery(id+"F12.wireOp",EDGE,"E6.bottom"),sQuery(id+"F12.wireOp",EDGE,"E6.top"),sQuery(id+"F12.wireOp",EDGE,"E6.left"),sQuery(id+"F12.wireOp",EDGE,"E6.right"),sQuery(id+"F12.wireOp",EDGE,"E7.bottom"),sQuery(id+"F12.wireOp",EDGE,"E7.top"),sQuery(id+"F12.wireOp",EDGE,"E7.right"),sQuery(id+"F12.wireOp",EDGE,"E8.bottom"),sQuery(id+"F12.wireOp",EDGE,"E8.top"),sQuery(id+"F12.wireOp",EDGE,"E8.right"),sQuery(id+"F12.wireOp",EDGE,"E9.bottom"),sQuery(id+"F12.wireOp",EDGE,"E9.top"),sQuery(id+"F12.wireOp",EDGE,"E9.right")])],"isStart":false});
            var sketch = newSketch(context, id + "F36", { "sketchPlane" : qUnion([Q0])});
            skLineSegment(sketch, "E21.bottom", {"start": v(-2444.75, 0) * mm, "end": v(-2527.3, 0) * mm});
            skLineSegment(sketch, "E21.top", {"start": v(-2444.75, 501.65) * mm, "end": v(-2527.3, 501.65) * mm});
            skLineSegment(sketch, "E21.left", {"start": v(-2444.75, 0) * mm, "end": v(-2444.75, 501.65) * mm});
            skLineSegment(sketch, "E21.right", {"start": v(-2527.3, 0) * mm, "end": v(-2527.3, 501.65) * mm});
            skSolve(sketch);
        }
        {
            var Q0;
            Q0 = qSketchRegion(id + "F36", true);
            var Q1;
            Q1=makeQuery(id+"F35.opExtrude","SWEPT_FACE",FACE,{"disambiguationData":[OSD([sQuery(id+"F34.wireOp",EDGE,"E20.right")])]});
            extrude(context, id + "F37", {"entities" : qUnion([Q0]), "operationType" : NewBodyOperationType.ADD, "endBound" : BoundingType.UP_TO_SURFACE, "depth" : 25.4 * mm, "endBoundEntityFace" : qUnion([Q1]), "offsetDistance" : 25.4 * mm});
        }
        {
            var Q0;
            Q0=makeQuery(id+"F33.opExtrude","CAP_FACE",FACE,{"disambiguationData":[OSD([sQuery(id+"F32.wireOp",EDGE,"E19.bottom"),sQuery(id+"F32.wireOp",EDGE,"E19.top"),sQuery(id+"F32.wireOp",EDGE,"E19.left"),sQuery(id+"F32.wireOp",EDGE,"E19.right")])],"isStart":false});
            var sketch = newSketch(context, id + "F38", { "sketchPlane" : qUnion([Q0])});
            skLineSegment(sketch, "E22.bottom", {"start": v(-6673.85, 0) * mm, "end": v(-6591.3, 0) * mm});
            skLineSegment(sketch, "E22.top", {"start": v(-6673.85, 501.65) * mm, "end": v(-6591.3, 501.65) * mm});
            skLineSegment(sketch, "E22.left", {"start": v(-6673.85, 0) * mm, "end": v(-6673.85, 501.65) * mm});
            skLineSegment(sketch, "E22.right", {"start": v(-6591.3, 0) * mm, "end": v(-6591.3, 501.65) * mm});
            skSolve(sketch);
        }
        {
            var Q0;
            Q0 = qSketchRegion(id + "F38", true);
            extrude(context, id + "F39", {"entities" : qUnion([Q0]), "operationType" : NewBodyOperationType.ADD, "endBound" : BoundingType.UP_TO_NEXT, "depth" : 25.4 * mm, "offsetDistance" : 25.4 * mm});
        }
    });
